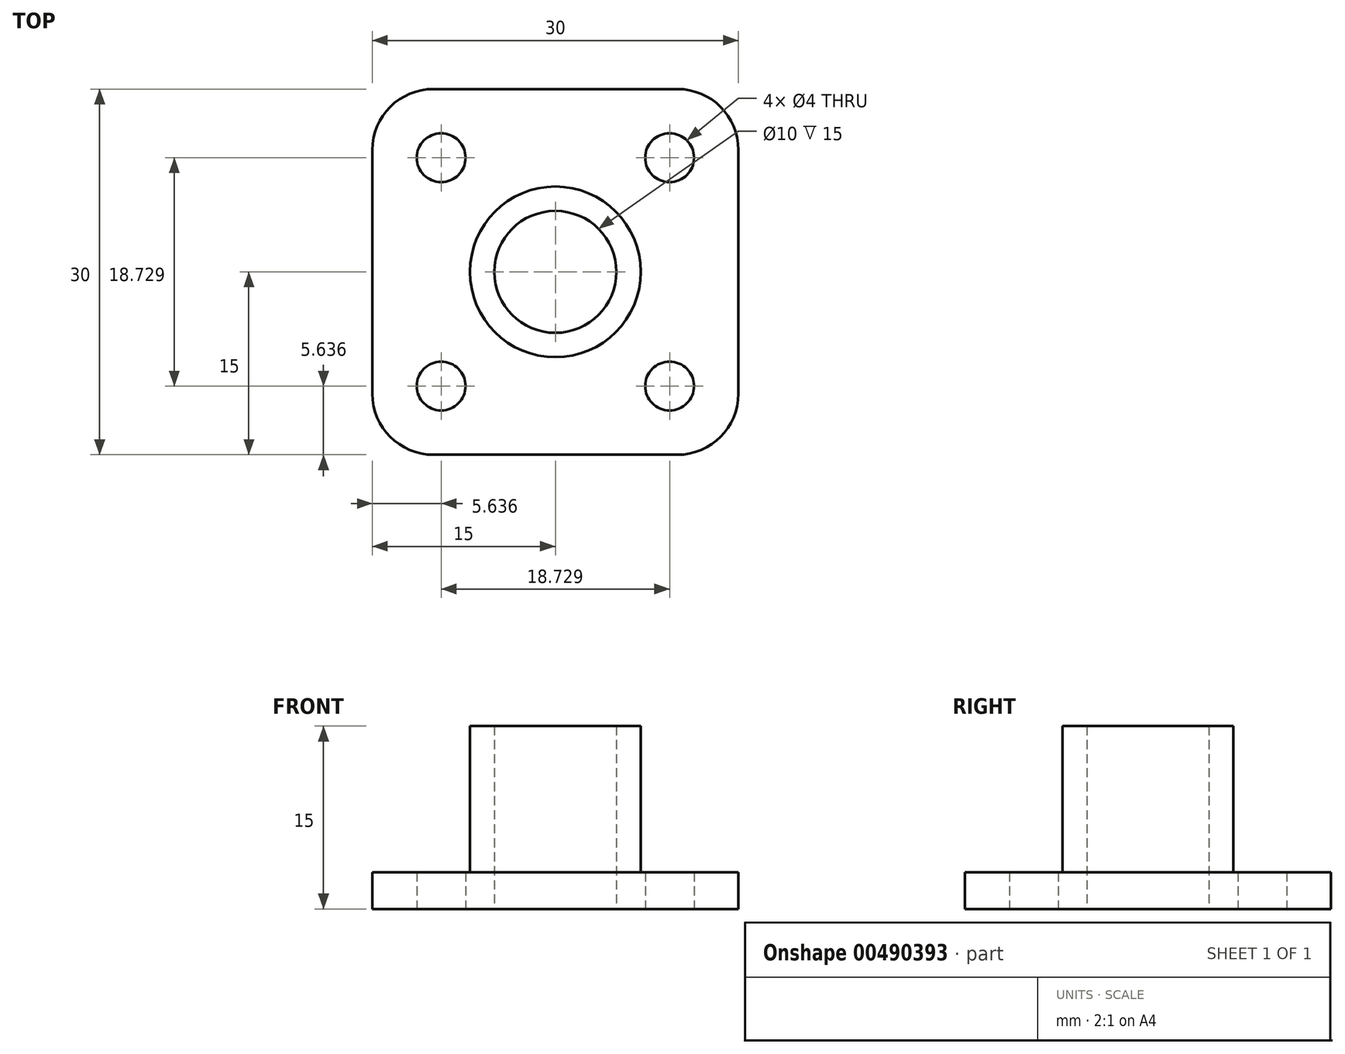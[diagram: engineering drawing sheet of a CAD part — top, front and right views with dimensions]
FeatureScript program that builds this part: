
annotation { "Feature Type Name" : "Feature", "Feature Type Description" : "" }
export const myFeature = defineFeature(function(context is Context, id is Id, definition is map)
    precondition{}
    {
        {
            var Q0;
            Q0=qCreatedBy(makeId("Top.planeOp"),FACE);
            var sketch = newSketch(context, id + "F0", { "sketchPlane" : qUnion([Q0])});
            skCircle(sketch, "E0", {"center": v(0, 0) * mm, "radius": 5 * mm});
            skCircle(sketch, "E1", {"center": v(0, 0) * mm, "radius": 7 * mm});
            skLineSegment(sketch, "E2.bottom", {"start": v(15, -15) * mm, "end": v(-15, -15) * mm});
            skLineSegment(sketch, "E2.top", {"start": v(15, 15) * mm, "end": v(-15, 15) * mm});
            skLineSegment(sketch, "E2.left", {"start": v(15, -15) * mm, "end": v(15, 15) * mm});
            skLineSegment(sketch, "E2.right", {"start": v(-15, -15) * mm, "end": v(-15, 15) * mm});
            skLineSegment(sketch, "E3", {"start": v(-15, 15) * mm, "end": v(0, 0) * mm, "construction": true});
            skCircle(sketch, "E4", {"center": v(-9.36, 9.36) * mm, "radius": 2 * mm});
            skCircle(sketch, "E5.1.0", {"center": v(-9.36, -9.36) * mm, "radius": 2 * mm});
            skCircle(sketch, "E5.2.0", {"center": v(9.36, -9.36) * mm, "radius": 2 * mm});
            skCircle(sketch, "E5.3.0", {"center": v(9.36, 9.36) * mm, "radius": 2 * mm});
            skSolve(sketch);
        }
        {
            var Q0;
            Q0=makeQuery(id+"F0.imprint","IMPRINT",FACE,{"disambiguationData":[TD([[makeQuery(id+"F0.imprint","IMPRINT",EDGE,{"derivedFrom":sQuery(id+"F0.wireOp",EDGE,"E1")}),-1.0]])]});
            var Q1;
            Q1=makeQuery(id+"F0.imprint","IMPRINT",FACE,{"disambiguationData":[TD([[makeQuery(id+"F0.imprint","IMPRINT",EDGE,{"derivedFrom":sQuery(id+"F0.wireOp",EDGE,"E0")}),-1.0]])]});
            extrude(context, id + "F1", {"entities" : qUnion([Q0, Q1]), "depth" : 3 * mm});
        }
        {
            var Q0;
            Q0=makeQuery(id+"F0.imprint","IMPRINT",FACE,{"disambiguationData":[TD([[makeQuery(id+"F0.imprint","IMPRINT",EDGE,{"derivedFrom":sQuery(id+"F0.wireOp",EDGE,"E0")}),-1.0]])]});
            extrude(context, id + "F2", {"entities" : qUnion([Q0]), "operationType" : NewBodyOperationType.ADD, "depth" : 15 * mm});
        }
        {
            var Q0;
            Q0=makeQuery(id+"F1.opExtrude","SWEPT_EDGE",EDGE,{"disambiguationData":[OSD([sQuery(id+"F0.wireOp",EDGE,"E2.top"),sQuery(id+"F0.wireOp",EDGE,"E2.right")])]});
            var Q1;
            Q1=makeQuery(id+"F1.opExtrude","SWEPT_EDGE",EDGE,{"disambiguationData":[OSD([sQuery(id+"F0.wireOp",EDGE,"E2.top"),sQuery(id+"F0.wireOp",EDGE,"E2.left")])]});
            var Q2;
            Q2=makeQuery(id+"F1.opExtrude","SWEPT_EDGE",EDGE,{"disambiguationData":[OSD([sQuery(id+"F0.wireOp",EDGE,"E2.bottom"),sQuery(id+"F0.wireOp",EDGE,"E2.right")])]});
            var Q3;
            Q3=makeQuery(id+"F1.opExtrude","SWEPT_EDGE",EDGE,{"disambiguationData":[OSD([sQuery(id+"F0.wireOp",EDGE,"E2.bottom"),sQuery(id+"F0.wireOp",EDGE,"E2.left")])]});
            fillet(context, id + "F3", {"entities" : qUnion([Q0, Q1, Q2, Q3]), "radius" : 5 * mm, "tangentPropagation" : true, "allowEdgeOverflow" : false});
        }
    });
